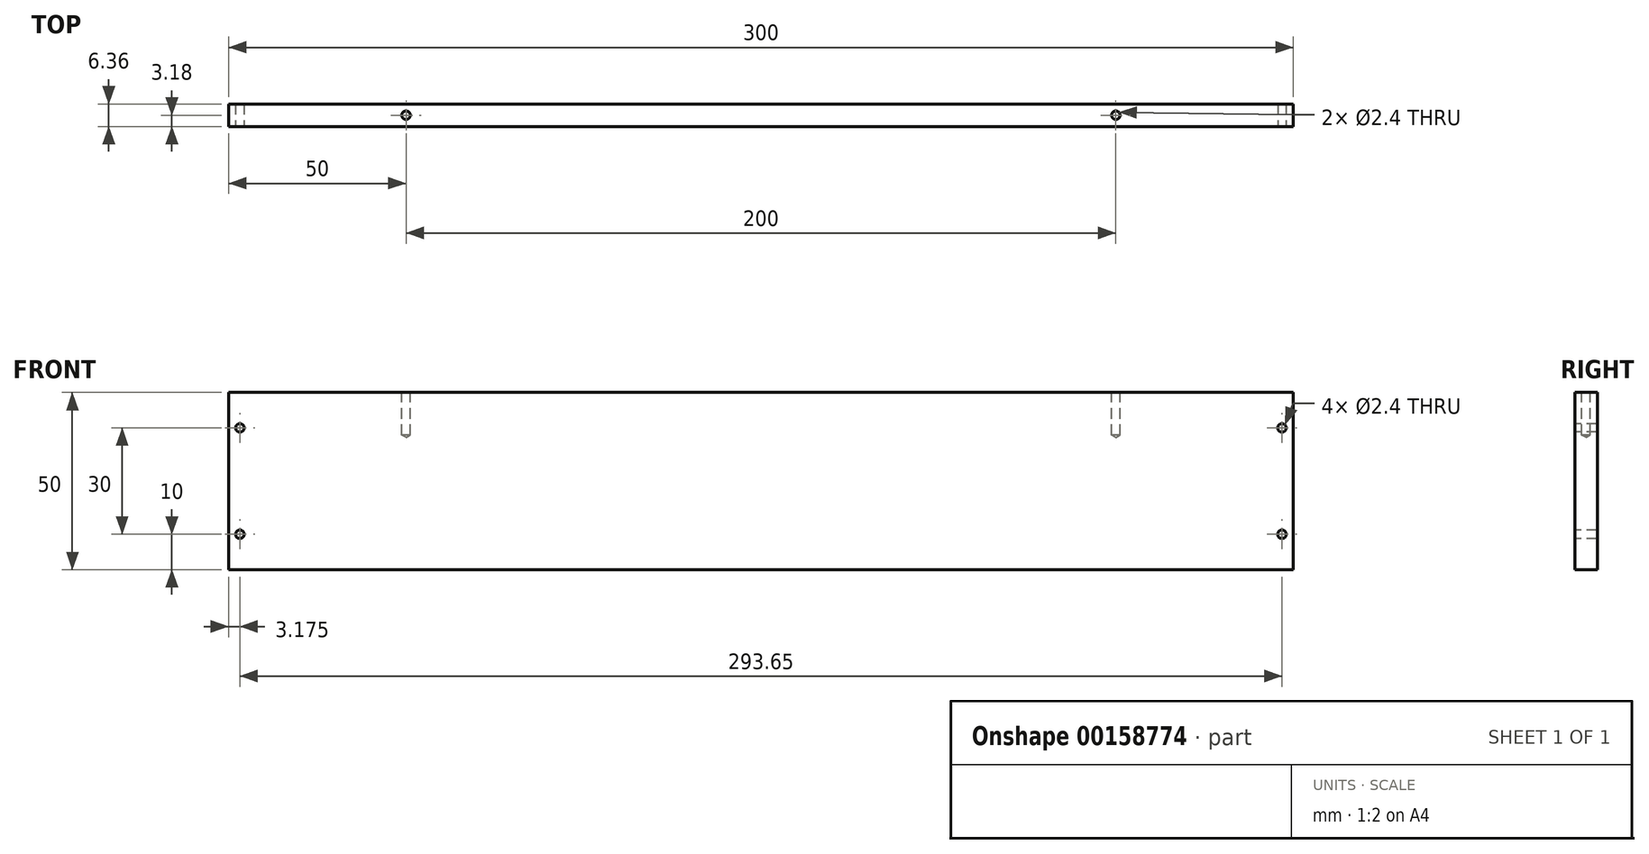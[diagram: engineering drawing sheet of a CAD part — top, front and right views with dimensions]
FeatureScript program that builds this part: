
annotation { "Feature Type Name" : "Feature", "Feature Type Description" : "" }
export const myFeature = defineFeature(function(context is Context, id is Id, definition is map)
    precondition{}
    {
        {
            var Q0;
            Q0=qCreatedBy(makeId("Front.planeOp"),FACE);
            var sketch = newSketch(context, id + "F0", { "sketchPlane" : qUnion([Q0])});
            skLineSegment(sketch, "E0.bottom", {"start": v(150, -25) * mm, "end": v(-150, -25) * mm});
            skLineSegment(sketch, "E0.top", {"start": v(150, 25) * mm, "end": v(-150, 25) * mm});
            skLineSegment(sketch, "E0.left", {"start": v(150, -25) * mm, "end": v(150, 25) * mm});
            skLineSegment(sketch, "E0.right", {"start": v(-150, -25) * mm, "end": v(-150, 25) * mm});
            skPoint(sketch, "E0.middle", {"position": v(0, 0) * mm});
            skSolve(sketch);
        }
        {
            var Q0;
            Q0 = qSketchRegion(id + "F0", true);
            extrude(context, id + "F1", {"entities" : qUnion([Q0]), "endBound" : BoundingType.SYMMETRIC, "depth" : 6.35 * mm});
        }
        {
            var Q0;
            Q0=makeQuery(id+"F1.opExtrude","CAP_FACE",FACE,{"disambiguationData":[OSD([sQuery(id+"F0.wireOp",EDGE,"E0.bottom"),sQuery(id+"F0.wireOp",EDGE,"E0.top"),sQuery(id+"F0.wireOp",EDGE,"E0.left"),sQuery(id+"F0.wireOp",EDGE,"E0.right")])],"isStart":false});
            var sketch = newSketch(context, id + "F2", { "sketchPlane" : qUnion([Q0])});
            skCircle(sketch, "E1", {"center": v(-146.82, -15) * mm, "radius": 1.5 * mm});
            skCircle(sketch, "E2.MirrorC", {"center": v(146.82, -15) * mm, "radius": 1.5 * mm});
            skCircle(sketch, "E3.MirrorC", {"center": v(-146.82, 15) * mm, "radius": 1.5 * mm});
            skCircle(sketch, "E4.MirrorC", {"center": v(146.82, 15) * mm, "radius": 1.5 * mm});
            skSolve(sketch);
        }
        {
            var Q0;
            Q0=sQuery(id+"F2.wireOp",VERTEX,"E3.MirrorC.center");
            var Q1;
            Q1=sQuery(id+"F2.wireOp",VERTEX,"E1.center");
            var Q2;
            Q2=sQuery(id+"F2.wireOp",VERTEX,"E4.MirrorC.center");
            var Q3;
            Q3=sQuery(id+"F2.wireOp",VERTEX,"E2.MirrorC.center");
            var Q4;
            Q4=makeQuery(id+"F1.opExtrude","SWEPT_BODY",BODY,{"disambiguationData":[OSD([sQuery(id+"F0.wireOp",EDGE,"E0.bottom"),sQuery(id+"F0.wireOp",EDGE,"E0.top"),sQuery(id+"F0.wireOp",EDGE,"E0.left"),sQuery(id+"F0.wireOp",EDGE,"E0.right")])]});
            hole(context, id + "F3", {"style" : HoleStyle.SIMPLE, "endStyle" : HoleEndStyle.THROUGH, "holeDiameter" : 2.4 * mm, "locations" : qUnion([Q0, Q1, Q2, Q3]), "scope" : qUnion([Q4]), "isTappedThrough" : true});
        }
        {
            var Q0;
            Q0=makeQuery(id+"F1.opExtrude","SWEPT_FACE",FACE,{"disambiguationData":[OSD([sQuery(id+"F0.wireOp",EDGE,"E0.top")])]});
            var sketch = newSketch(context, id + "F4", { "sketchPlane" : qUnion([Q0])});
            skCircle(sketch, "E5", {"center": v(-100, 0) * mm, "radius": 1.5 * mm});
            skCircle(sketch, "E6.MirrorC", {"center": v(100, 0) * mm, "radius": 1.5 * mm});
            skSolve(sketch);
        }
        {
            var Q0;
            Q0=sQuery(id+"F4.wireOp",VERTEX,"E5.center");
            var Q1;
            Q1=sQuery(id+"F4.wireOp",VERTEX,"E6.MirrorC.center");
            var Q2;
            Q2=makeQuery(id+"F1.opExtrude","SWEPT_BODY",BODY,{"disambiguationData":[OSD([sQuery(id+"F0.wireOp",EDGE,"E0.bottom"),sQuery(id+"F0.wireOp",EDGE,"E0.top"),sQuery(id+"F0.wireOp",EDGE,"E0.left"),sQuery(id+"F0.wireOp",EDGE,"E0.right")])]});
            hole(context, id + "F5", {"style" : HoleStyle.SIMPLE, "endStyle" : HoleEndStyle.BLIND, "standardTappedOrClearance" : lookupTablePath({ "standard" : "ISO", "engagement" : "75%", "pitch" : "0.6 mm", "size" : "M3", "type" : "Tapped" }), "standardBlindInLast" : lookupTablePath({ "standard" : "ISO", "engagement" : "75%", "pitch" : "0.6 mm", "size" : "M3", "type" : "Tapped" }), "holeDiameter" : 2.4 * mm, "holeDepth" : 12 * mm, "locations" : qUnion([Q0, Q1]), "scope" : qUnion([Q2])});
        }
    });
